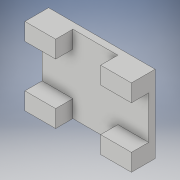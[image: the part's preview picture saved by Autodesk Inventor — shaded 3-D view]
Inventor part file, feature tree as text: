
AUTODESK INVENTOR PART (.ipt)
format: ipt  version: 2018 (Build 220112000, 112)  size: 117,760 bytes
history: native  units: in
note: dims shown in document units (in); Inventor stores cm internally (conversion verified against a paired STEP export)
features: extrude x2, sketch x2
ambient origin geometry x8: Origin, YZ Plane, XZ Plane, XY Plane, X Axis, Y Axis, Z Axis, Center Point
bodies: Solid1 (feature_tree)
feature tree (4):
  extrude  "Extrusion1"  Depth=2.87in
  extrude  "Extrusion2"  Depth=1.14in
  sketch  "Sketch1"  dims[d0=3.95in d1=2.87in]
  sketch  "Sketch2"  dims[d2=0.24in d3=0.0in d4=1.14in d5=0.64in d6=0.64in d7=0.0in]
